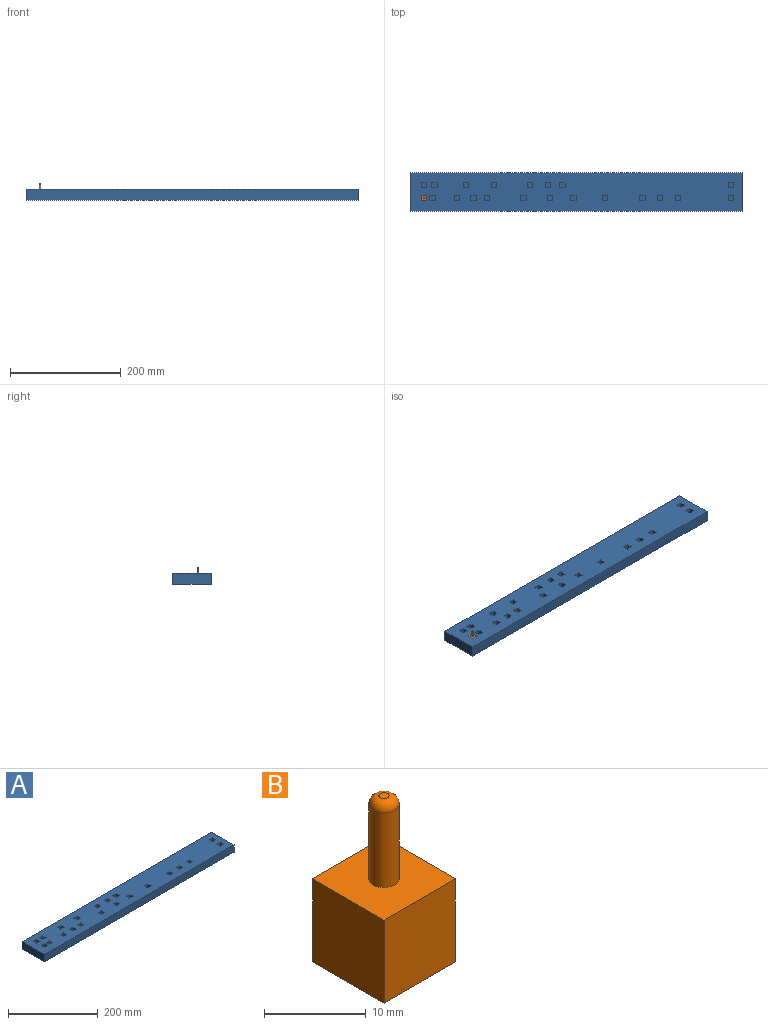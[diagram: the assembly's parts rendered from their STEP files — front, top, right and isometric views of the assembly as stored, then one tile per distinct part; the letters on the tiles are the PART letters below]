
ASSEMBLY  parts=2 mates=1
PART A: 111 faces, bbox 600x70x20 mm
  f0: plane 10x10mm, normal (0,-1,0), area 100mm2, adj f1,f87,f88,f89
  f1: plane 10x10mm, normal (-1,0,0), area 100mm2, adj f0,f2,f88,f89
  f2: plane 10x10mm, normal (0,1,0), area 100mm2, adj f1,f87,f88,f89
  f3: plane 10x10mm, normal (1,0,0), area 100mm2, adj f4,f66,f88,f109
  f4: plane 10x10mm, normal (0,-1,0), area 100mm2, adj f3,f5,f88,f109
  f5: plane 10x10mm, normal (-1,0,0), area 100mm2, adj f4,f66,f88,f109
  f6: plane 10x10mm, normal (1,0,0), area 100mm2, adj f7,f67,f88,f108
  f7: plane 10x10mm, normal (0,-1,0), area 100mm2, adj f6,f8,f88,f108
  f8: plane 10x10mm, normal (-1,0,0), area 100mm2, adj f7,f67,f88,f108
  f9: plane 10x10mm, normal (1,0,0), area 100mm2, adj f10,f68,f88,f107
  f10: plane 10x10mm, normal (0,-1,0), area 100mm2, adj f9,f11,f88,f107
  f11: plane 10x10mm, normal (-1,0,0), area 100mm2, adj f10,f68,f88,f107
  f12: plane 10x10mm, normal (1,0,0), area 100mm2, adj f13,f69,f88,f106
  f13: plane 10x10mm, normal (0,-1,0), area 100mm2, adj f12,f14,f88,f106
  f14: plane 10x10mm, normal (-1,0,0), area 100mm2, adj f13,f69,f88,f106
  f15: plane 10x10mm, normal (1,0,0), area 100mm2, adj f16,f70,f88,f105
  f16: plane 10x10mm, normal (0,-1,0), area 100mm2, adj f15,f17,f88,f105
  f17: plane 10x10mm, normal (-1,0,0), area 100mm2, adj f16,f70,f88,f105
  f18: plane 10x10mm, normal (1,0,0), area 100mm2, adj f19,f71,f88,f104
  f19: plane 10x10mm, normal (0,-1,0), area 100mm2, adj f18,f20,f88,f104
  f20: plane 10x10mm, normal (-1,0,0), area 100mm2, adj f19,f71,f88,f104
  f21: plane 10x10mm, normal (1,0,0), area 100mm2, adj f22,f72,f88,f103
  f22: plane 10x10mm, normal (0,-1,0), area 100mm2, adj f21,f23,f88,f103
  f23: plane 10x10mm, normal (-1,0,0), area 100mm2, adj f22,f72,f88,f103
  f24: plane 10x10mm, normal (1,0,0), area 100mm2, adj f25,f73,f88,f102
  f25: plane 10x10mm, normal (0,-1,0), area 100mm2, adj f24,f26,f88,f102
  f26: plane 10x10mm, normal (-1,0,0), area 100mm2, adj f25,f73,f88,f102
  f27: plane 10x10mm, normal (1,0,0), area 100mm2, adj f28,f74,f88,f101
  f28: plane 10x10mm, normal (0,-1,0), area 100mm2, adj f27,f29,f88,f101
  f29: plane 10x10mm, normal (-1,0,0), area 100mm2, adj f28,f74,f88,f101
  f30: plane 10x10mm, normal (1,0,0), area 100mm2, adj f31,f75,f88,f100
  f31: plane 10x10mm, normal (0,-1,0), area 100mm2, adj f30,f32,f88,f100
  f32: plane 10x10mm, normal (-1,0,0), area 100mm2, adj f31,f75,f88,f100
  f33: plane 10x10mm, normal (1,0,0), area 100mm2, adj f34,f76,f88,f99
  f34: plane 10x10mm, normal (0,-1,0), area 100mm2, adj f33,f35,f88,f99
  f35: plane 10x10mm, normal (-1,0,0), area 100mm2, adj f34,f76,f88,f99
  f36: plane 10x10mm, normal (1,0,0), area 100mm2, adj f37,f77,f88,f98
  f37: plane 10x10mm, normal (0,-1,0), area 100mm2, adj f36,f38,f88,f98
  f38: plane 10x10mm, normal (-1,0,0), area 100mm2, adj f37,f77,f88,f98
  f39: plane 10x10mm, normal (-1,0,0), area 100mm2, adj f40,f78,f88,f97
  f40: plane 10x10mm, normal (0,1,0), area 100mm2, adj f39,f41,f88,f97
  f41: plane 10x10mm, normal (1,0,0), area 100mm2, adj f40,f78,f88,f97
  f42: plane 10x10mm, normal (0,1,0), area 100mm2, adj f43,f79,f88,f96
  f43: plane 10x10mm, normal (1,0,0), area 100mm2, adj f42,f44,f88,f96
  f44: plane 10x10mm, normal (0,-1,0), area 100mm2, adj f43,f79,f88,f96
  f45: plane 10x10mm, normal (0,1,0), area 100mm2, adj f46,f80,f88,f95
  f46: plane 10x10mm, normal (1,0,0), area 100mm2, adj f45,f47,f88,f95
  f47: plane 10x10mm, normal (0,-1,0), area 100mm2, adj f46,f80,f88,f95
  f48: plane 10x10mm, normal (0,1,0), area 100mm2, adj f49,f81,f88,f94
  f49: plane 10x10mm, normal (1,0,0), area 100mm2, adj f48,f50,f88,f94
  f50: plane 10x10mm, normal (0,-1,0), area 100mm2, adj f49,f81,f88,f94
  f51: plane 600x20mm, normal (0,-1,0), area 12000mm2, adj f52,f82,f88,f110
  f52: plane 70x20mm, normal (1,0,0), area 1400mm2, adj f51,f53,f88,f110
  f53: plane 600x20mm, normal (0,1,0), area 12000mm2, adj f52,f82,f88,f110
  f54: plane 10x10mm, normal (0,1,0), area 100mm2, adj f55,f83,f88,f93
  f55: plane 10x10mm, normal (1,0,0), area 100mm2, adj f54,f56,f88,f93
  f56: plane 10x10mm, normal (0,-1,0), area 100mm2, adj f55,f83,f88,f93
  f57: plane 10x10mm, normal (0,1,0), area 100mm2, adj f58,f84,f88,f92
  f58: plane 10x10mm, normal (1,0,0), area 100mm2, adj f57,f59,f88,f92
  f59: plane 10x10mm, normal (0,-1,0), area 100mm2, adj f58,f84,f88,f92
  f60: plane 10x10mm, normal (0,1,0), area 100mm2, adj f61,f85,f88,f91
  f61: plane 10x10mm, normal (1,0,0), area 100mm2, adj f60,f62,f88,f91
  f62: plane 10x10mm, normal (0,-1,0), area 100mm2, adj f61,f85,f88,f91
  f63: plane 10x10mm, normal (0,1,0), area 100mm2, adj f64,f86,f88,f90
  f64: plane 10x10mm, normal (1,0,0), area 100mm2, adj f63,f65,f88,f90
  f65: plane 10x10mm, normal (0,-1,0), area 100mm2, adj f64,f86,f88,f90
  f66: plane 10x10mm, normal (0,1,0), area 100mm2, adj f3,f5,f88,f109
  f67: plane 10x10mm, normal (0,1,0), area 100mm2, adj f6,f8,f88,f108
  f68: plane 10x10mm, normal (0,1,0), area 100mm2, adj f9,f11,f88,f107
  f69: plane 10x10mm, normal (0,1,0), area 100mm2, adj f12,f14,f88,f106
  f70: plane 10x10mm, normal (0,1,0), area 100mm2, adj f15,f17,f88,f105
  f71: plane 10x10mm, normal (0,1,0), area 100mm2, adj f18,f20,f88,f104
  f72: plane 10x10mm, normal (0,1,0), area 100mm2, adj f21,f23,f88,f103
  f73: plane 10x10mm, normal (0,1,0), area 100mm2, adj f24,f26,f88,f102
  f74: plane 10x10mm, normal (0,1,0), area 100mm2, adj f27,f29,f88,f101
  f75: plane 10x10mm, normal (0,1,0), area 100mm2, adj f30,f32,f88,f100
  f76: plane 10x10mm, normal (0,1,0), area 100mm2, adj f33,f35,f88,f99
  f77: plane 10x10mm, normal (0,1,0), area 100mm2, adj f36,f38,f88,f98
  f78: plane 10x10mm, normal (0,-1,0), area 100mm2, adj f39,f41,f88,f97
  f79: plane 10x10mm, normal (-1,0,0), area 100mm2, adj f42,f44,f88,f96
  f80: plane 10x10mm, normal (-1,0,0), area 100mm2, adj f45,f47,f88,f95
  f81: plane 10x10mm, normal (-1,0,0), area 100mm2, adj f48,f50,f88,f94
  f82: plane 70x20mm, normal (-1,0,0), area 1400mm2, adj f51,f53,f88,f110
  f83: plane 10x10mm, normal (-1,0,0), area 100mm2, adj f54,f56,f88,f93
  f84: plane 10x10mm, normal (-1,0,0), area 100mm2, adj f57,f59,f88,f92
  f85: plane 10x10mm, normal (-1,0,0), area 100mm2, adj f60,f62,f88,f91
  f86: plane 10x10mm, normal (-1,0,0), area 100mm2, adj f63,f65,f88,f90
  f87: plane 10x10mm, normal (1,0,0), area 100mm2, adj f0,f2,f88,f89
  f88: plane 600x70mm, normal (0,0,1), area 39900mm2, adj f0,f1,f2,f3,f4,f5,f6,f7
  f89: plane 10x10mm, normal (0,0,1), area 100mm2, adj f0,f1,f2,f87
  f90: plane 10x10mm, normal (0,0,1), area 100mm2, adj f63,f64,f65,f86
  f91: plane 10x10mm, normal (0,0,1), area 100mm2, adj f60,f61,f62,f85
  f92: plane 10x10mm, normal (0,0,1), area 100mm2, adj f57,f58,f59,f84
  f93: plane 10x10mm, normal (0,0,1), area 100mm2, adj f54,f55,f56,f83
  f94: plane 10x10mm, normal (0,0,1), area 100mm2, adj f48,f49,f50,f81
  f95: plane 10x10mm, normal (0,0,1), area 100mm2, adj f45,f46,f47,f80
  f96: plane 10x10mm, normal (0,0,1), area 100mm2, adj f42,f43,f44,f79
  f97: plane 10x10mm, normal (0,0,1), area 100mm2, adj f39,f40,f41,f78
  f98: plane 10x10mm, normal (0,0,1), area 100mm2, adj f36,f37,f38,f77
  f99: plane 10x10mm, normal (0,0,1), area 100mm2, adj f33,f34,f35,f76
  f100: plane 10x10mm, normal (0,0,1), area 100mm2, adj f30,f31,f32,f75
  f101: plane 10x10mm, normal (0,0,1), area 100mm2, adj f27,f28,f29,f74
  f102: plane 10x10mm, normal (0,0,1), area 100mm2, adj f24,f25,f26,f73
  f103: plane 10x10mm, normal (0,0,1), area 100mm2, adj f21,f22,f23,f72
  f104: plane 10x10mm, normal (0,0,1), area 100mm2, adj f18,f19,f20,f71
  f105: plane 10x10mm, normal (0,0,1), area 100mm2, adj f15,f16,f17,f70
  f106: plane 10x10mm, normal (0,0,1), area 100mm2, adj f12,f13,f14,f69
  f107: plane 10x10mm, normal (0,0,1), area 100mm2, adj f9,f10,f11,f68
  f108: plane 10x10mm, normal (0,0,1), area 100mm2, adj f6,f7,f8,f67
  f109: plane 10x10mm, normal (0,0,1), area 100mm2, adj f3,f4,f5,f66
  f110: plane 600x70mm, normal (0,0,-1), area 42000mm2, adj f51,f52,f53,f82
PART B: 9 faces, bbox 10x10x20 mm
  f0: plane 10x9.95mm, normal (-1,0,0), area 99.5mm2, adj f1,f3,f4,f5
  f1: plane 10x9.95mm, normal (0,-1,0), area 99.5mm2, adj f0,f2,f4,f5
  f2: plane 10x9.95mm, normal (1,0,0), area 99.5mm2, adj f1,f3,f4,f5
  f3: plane 10x9.95mm, normal (0,1,0), area 99.5mm2, adj f0,f2,f4,f5
  f4: plane 9.95x9.95mm, normal (0,0,1), area 91.9mm2, adj f0,f1,f2,f3,f6
  f5: plane 9.95x9.95mm, normal (0,0,-1), area 99mm2, adj f0,f1,f2,f3
  f6: cylinder r=1.5mm len=9mm, axis (0,0,-1), area 84.8mm2, adj f4,f8
  f7: plane 1x1mm, normal (0,0,1), area 0.8mm2, adj f8
  f8: torus R=0.5mm, axis (0,0,1), area 11.2mm2, adj f6,f7
PLACE A t=(0,0,-10)mm
PLACE B t=(20.02,19.03,-9.3)mm
MATE slider B.f6 <-> A.f88  axis (0,0,1) through (25,24,0.7)mm
